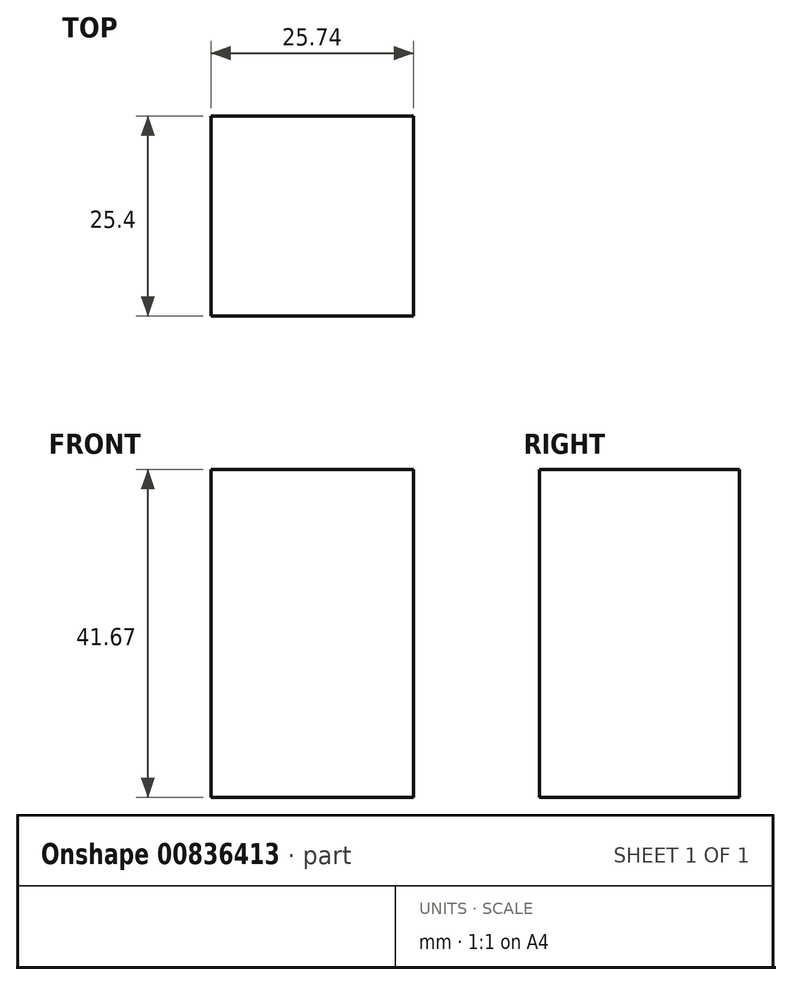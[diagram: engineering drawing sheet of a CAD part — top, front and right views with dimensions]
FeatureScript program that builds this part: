
annotation { "Feature Type Name" : "Feature", "Feature Type Description" : "" }
export const myFeature = defineFeature(function(context is Context, id is Id, definition is map)
    precondition{}
    {
        {
            var Q0;
            Q0=qCreatedBy(makeId("Front.planeOp"),FACE);
            var sketch = newSketch(context, id + "F0", { "sketchPlane" : qUnion([Q0])});
            skLineSegment(sketch, "E0.bottom", {"start": v(28.93, 41.67) * mm, "end": v(54.67, 41.67) * mm});
            skLineSegment(sketch, "E0.top", {"start": v(28.93, 0) * mm, "end": v(54.67, 0) * mm});
            skLineSegment(sketch, "E0.left", {"start": v(28.93, 41.67) * mm, "end": v(28.93, 0) * mm});
            skLineSegment(sketch, "E0.right", {"start": v(54.67, 41.67) * mm, "end": v(54.67, 0) * mm});
            skSolve(sketch);
        }
        {
            var Q0;
            Q0=makeQuery(id+"F0.imprint","IMPRINT",FACE,{"disambiguationData":[TD([[makeQuery(id+"F0.imprint","IMPRINT",EDGE,{"derivedFrom":sQuery(id+"F0.wireOp",EDGE,"E0.bottom")}),-1.0]])]});
            extrude(context, id + "F1", {"entities" : qUnion([Q0]), "depth" : 25.4 * mm, "offsetDistance" : 25.4 * mm});
        }
    });
